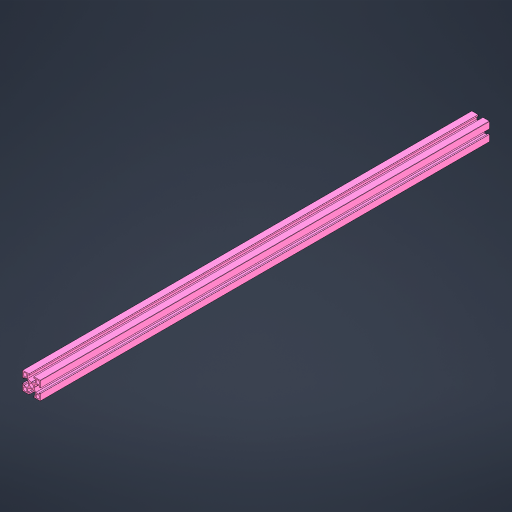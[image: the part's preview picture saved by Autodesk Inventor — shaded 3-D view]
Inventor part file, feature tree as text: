
AUTODESK INVENTOR PART (.ipt)
format: ipt  version: 2024 (Build 280153000, 153)  size: 368,128 bytes
history: native  units: mm
features: other x3, extrude x1, fillet x1, sketch x1
ambient origin geometry x8: Origin, YZ Plane, XZ Plane, XY Plane, X Axis, Y Axis, Z Axis, Center Point
bodies: Body1 (feature_tree)
feature tree (6):
  other  "솔리드1"
  extrude  "프로파일 길이 설정"  Depth=20.0mm
  fillet  "모서리"  Radius=20.0mm
  sketch  "스케치1"
  other  "Finish1"
  other  "Finish2"
